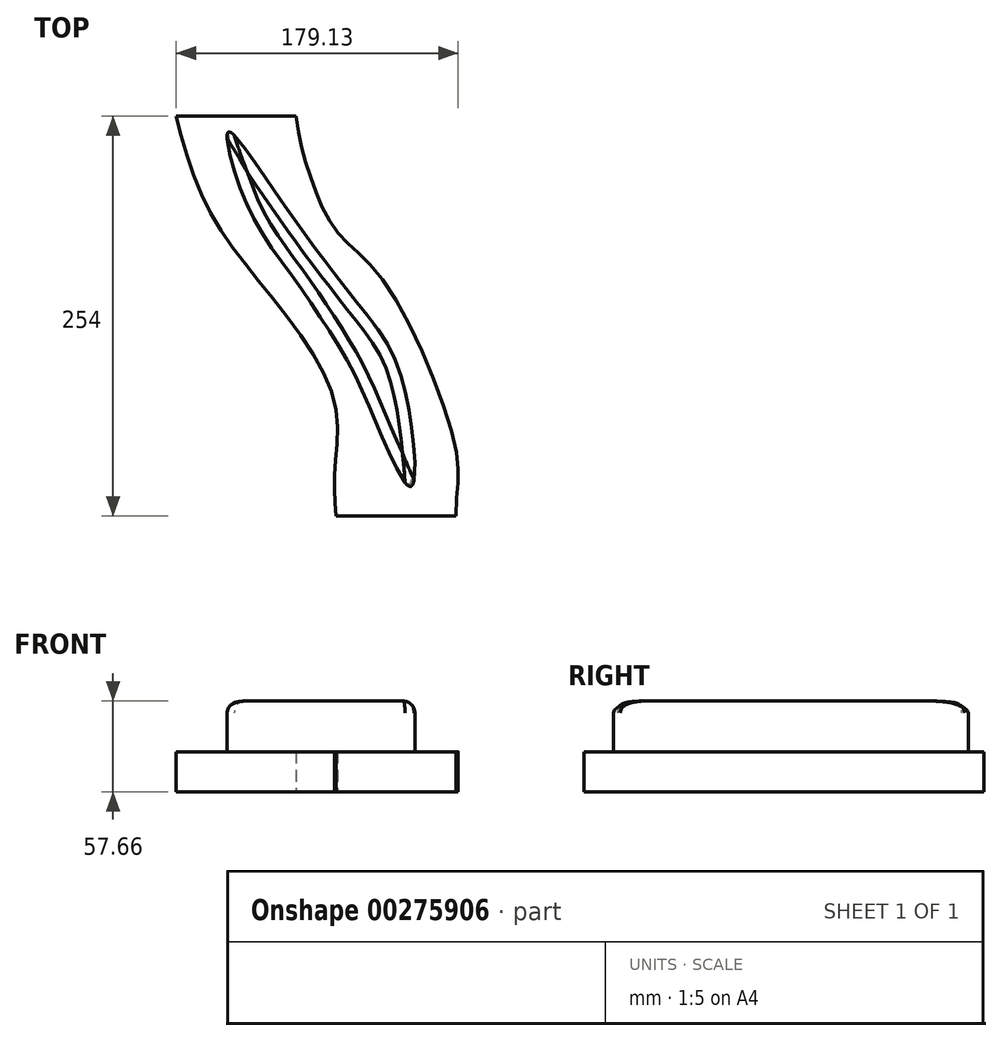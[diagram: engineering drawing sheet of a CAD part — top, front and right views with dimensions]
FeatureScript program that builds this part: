
annotation { "Feature Type Name" : "Feature", "Feature Type Description" : "" }
export const myFeature = defineFeature(function(context is Context, id is Id, definition is map)
    precondition{}
    {
        {
            var Q0;
            Q0=qCreatedBy(makeId("Top.planeOp"),FACE);
            var sketch = newSketch(context, id + "F0", { "sketchPlane" : qUnion([Q0])});
            skLineSegment(sketch, "E0", {"start": v(-177.8, 167.28) * mm, "end": v(-101.6, 167.28) * mm});
            skLineSegment(sketch, "E1", {"start": v(-177.8, 167.28) * mm, "end": v(-177.8, -86.72) * mm});
            skLineSegment(sketch, "E2", {"start": v(-177.8, -86.72) * mm, "end": v(-76.2, -86.72) * mm});
            skLineSegment(sketch, "E3", {"start": v(-76.2, -86.72) * mm, "end": v(0, -86.72) * mm});
            skFitSpline(sketch, "E4", {"points": [v(-177.8, 167.28) * mm, v(-155.8, 105.35) * mm, v(-114.47, 49.09) * mm, v(-77.34, -14.07) * mm, v(-76.96, -56.94) * mm, v(-76.2, -86.72) * mm], "startDerivative": vector(70.16, -280.87) * mm, "endDerivative": vector(18.93, -180.07) * mm});
            skFitSpline(sketch, "E5", {"points": [v(-101.6, 167.28) * mm, v(-92.65, 129.09) * mm, v(-75.43, 93.49) * mm, v(-45.96, 62.49) * mm, v(0, -45.46) * mm, v(0, -86.72) * mm], "startDerivative": vector(28.61, -236.54) * mm, "endDerivative": vector(0, -304.4) * mm});
            skFitSpline(sketch, "E6", {"points": [v(-144.7, 157.03) * mm, v(-133.48, 112.68) * mm, v(-105.67, 67.84) * mm, v(-73.13, 18.85) * mm, v(-54.76, -18.28) * mm, v(-28.73, -68.04) * mm, v(-33.32, -3.35) * mm, v(-57.44, 41.82) * mm, v(-110.47, 112.72) * mm, v(-144.7, 157.03) * mm]});
            skSolve(sketch);
        }
        {
            var Q0;
            Q0=makeQuery(id+"F0.imprint","IMPRINT",FACE,{"disambiguationData":[TD([[makeQuery(id+"F0.imprint","IMPRINT",EDGE,{"derivedFrom":sQuery(id+"F0.wireOp",EDGE,"E0")}),-1.0]])]});
            extrude(context, id + "F1", {"entities" : qUnion([Q0]), "depth" : 25.4 * mm});
        }
        {
            var Q0;
            Q0=makeQuery(id+"F0.imprint","IMPRINT",FACE,{"disambiguationData":[TD([[makeQuery(id+"F0.imprint","IMPRINT",EDGE,{"derivedFrom":sQuery(id+"F0.wireOp",EDGE,"E6")}),1.0]])]});
            extrude(context, id + "F2", {"entities" : qUnion([Q0]), "operationType" : NewBodyOperationType.ADD, "depth" : 57.66 * mm});
        }
        {
            var Q0;
            Q0=makeQuery(id+"F2.opExtrude","CAP_EDGE",EDGE,{"disambiguationData":[OSD([sQuery(id+"F0.wireOp",EDGE,"E6")])],"isStart":false});
            fillet(context, id + "F3", {"entities" : qUnion([Q0]), "radius" : 7.62 * mm, "tangentPropagation" : true, "allowEdgeOverflow" : false});
        }
    });
